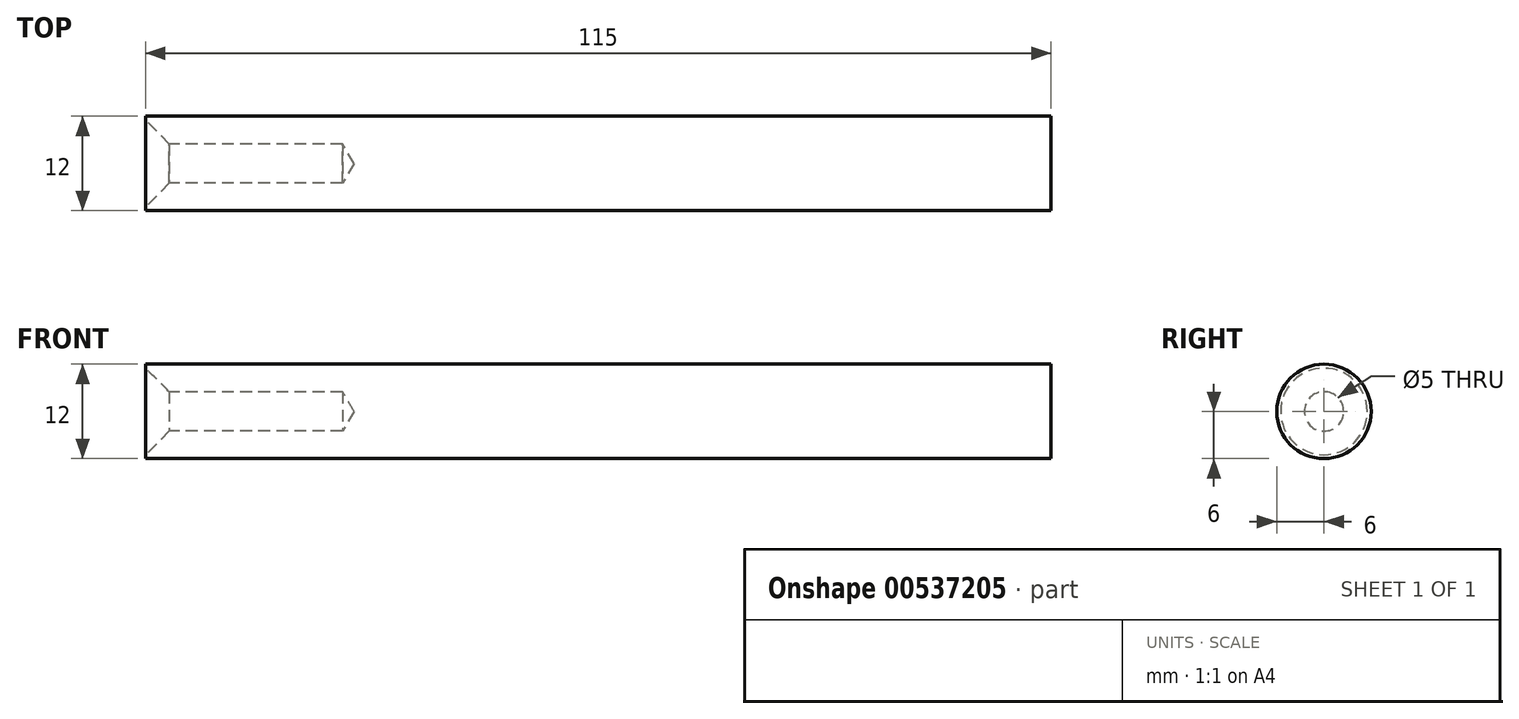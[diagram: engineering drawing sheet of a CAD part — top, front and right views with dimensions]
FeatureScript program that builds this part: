
annotation { "Feature Type Name" : "Feature", "Feature Type Description" : "" }
export const myFeature = defineFeature(function(context is Context, id is Id, definition is map)
    precondition{}
    {
        {
            var Q0;
            Q0=qCreatedBy(makeId("Right.planeOp"),FACE);
            var sketch = newSketch(context, id + "F0", { "sketchPlane" : qUnion([Q0])});
            skCircle(sketch, "E0", {"center": v(0, 0) * mm, "radius": 6 * mm});
            skSolve(sketch);
        }
        {
            var Q0;
            Q0=makeQuery(id+"F0.imprint","IMPRINT",FACE,{"disambiguationData":[TD([[makeQuery(id+"F0.imprint","IMPRINT",EDGE,{"derivedFrom":sQuery(id+"F0.wireOp",EDGE,"E0")}),1.0]])]});
            extrude(context, id + "F1", {"entities" : qUnion([Q0]), "depth" : 115 * mm, "offsetDistance" : 25 * mm});
        }
        {
            var Q0;
            Q0=makeQuery(id+"F1.opExtrude","CAP_FACE",FACE,{"disambiguationData":[OSD([sQuery(id+"F0.wireOp",EDGE,"E0")])],"isStart":true});
            var sketch = newSketch(context, id + "F2", { "sketchPlane" : qUnion([Q0])});
            skPoint(sketch, "E1", {"position": v(0, 0) * mm});
            skSolve(sketch);
        }
        {
            var Q0;
            Q0=sQuery(id+"F2.wireOp",VERTEX,"E1");
            var Q1;
            Q1=makeQuery(id+"F1.opExtrude","SWEPT_BODY",BODY,{"disambiguationData":[OSD([sQuery(id+"F0.wireOp",EDGE,"E0")])]});
            hole(context, id + "F3", {"style" : HoleStyle.C_SINK, "endStyle" : HoleEndStyle.BLIND, "holeDiameter" : 5 * mm, "cSinkDiameter" : 11 * mm, "cSinkAngle" : 90 * degree, "holeDepth" : 25 * mm, "isTappedThrough" : true, "tappedDepth" : 12 * mm, "tapClearance" : 3, "locations" : qUnion([Q0]), "scope" : qUnion([Q1])});
        }
    });
